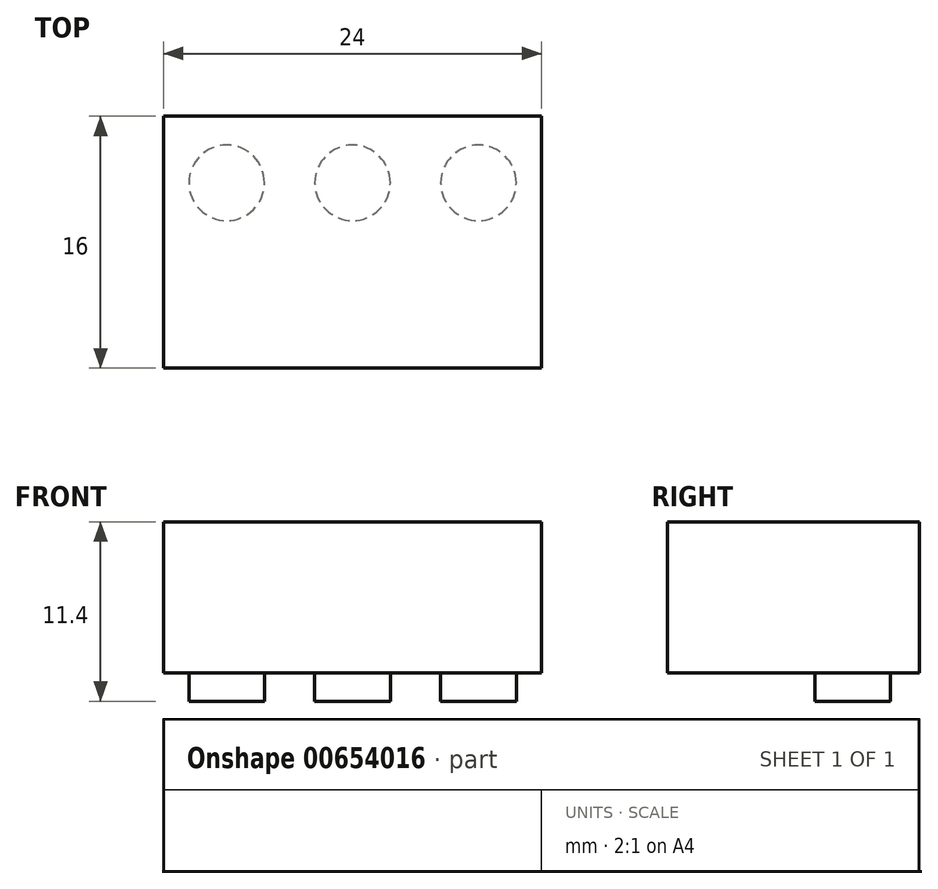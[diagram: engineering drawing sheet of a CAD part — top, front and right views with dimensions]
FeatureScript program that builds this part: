
annotation { "Feature Type Name" : "Feature", "Feature Type Description" : "" }
export const myFeature = defineFeature(function(context is Context, id is Id, definition is map)
    precondition{}
    {
        {
            var Q0;
            Q0=qCreatedBy(makeId("Top.planeOp"),FACE);
            var sketch = newSketch(context, id + "F0", { "sketchPlane" : qUnion([Q0])});
            skLineSegment(sketch, "E0.bottom", {"start": v(0, 0) * mm, "end": v(-24, 0) * mm});
            skLineSegment(sketch, "E0.top", {"start": v(0, 16) * mm, "end": v(-24, 16) * mm});
            skLineSegment(sketch, "E0.left", {"start": v(0, 0) * mm, "end": v(0, 16) * mm});
            skLineSegment(sketch, "E0.right", {"start": v(-24, 0) * mm, "end": v(-24, 16) * mm});
            skSolve(sketch);
        }
        {
            var Q0;
            Q0=makeQuery(id+"F0.imprint","IMPRINT",FACE,{"disambiguationData":[TD([[makeQuery(id+"F0.imprint","IMPRINT",EDGE,{"derivedFrom":sQuery(id+"F0.wireOp",EDGE,"E0.bottom")}),-1.0]])]});
            extrude(context, id + "F1", {"entities" : qUnion([Q0]), "depth" : 9.6 * mm, "offsetDistance" : 25.4 * mm});
        }
        {
            var Q0;
            Q0=qCreatedBy(makeId("Top.planeOp"),FACE);
            var sketch = newSketch(context, id + "F2", { "sketchPlane" : qUnion([Q0])});
            skLineSegment(sketch, "E1", {"start": v(-24.04, 7.52) * mm, "end": v(0, 7.52) * mm, "construction": true});
            skLineSegment(sketch, "E2", {"start": v(-16, 15.97) * mm, "end": v(-16, 0) * mm});
            skLineSegment(sketch, "E3", {"start": v(-8, 16.03) * mm, "end": v(-8, 0) * mm, "construction": true});
            skLineSegment(sketch, "E4", {"start": v(-23.99, 16.03) * mm, "end": v(-16, 7.52) * mm, "construction": true});
            skPoint(sketch, "E4.endSnap0", {"position": v(-16, 7.99) * mm});
            skLineSegment(sketch, "E5", {"start": v(-16, 7.52) * mm, "end": v(-8, 16.03) * mm, "construction": true});
            skLineSegment(sketch, "E6", {"start": v(-8, 16.03) * mm, "end": v(0, 7.52) * mm, "construction": true});
            skCircle(sketch, "E7", {"center": v(-20, 11.77) * mm, "radius": 2.4 * mm});
            skCircle(sketch, "E8", {"center": v(-12, 11.77) * mm, "radius": 2.4 * mm});
            skCircle(sketch, "E9", {"center": v(-4, 11.77) * mm, "radius": 2.4 * mm});
            skCircle(sketch, "E10.MirrorC", {"center": v(-20, 3.26) * mm, "radius": 2.4 * mm});
            skCircle(sketch, "E11.MirrorC", {"center": v(-12, 3.26) * mm, "radius": 2.4 * mm});
            skCircle(sketch, "E12.MirrorC", {"center": v(-4, 3.26) * mm, "radius": 2.4 * mm});
            skSolve(sketch);
        }
        {
            var Q0;
            Q0=makeQuery(id+"F2.imprint","IMPRINT",FACE,{"disambiguationData":[TD([[makeQuery(id+"F2.imprint","IMPRINT",EDGE,{"derivedFrom":sQuery(id+"F2.wireOp",EDGE,"E10.MirrorC")}),-1.0]])]});
            var Q1;
            Q1=makeQuery(id+"F2.imprint","IMPRINT",FACE,{"disambiguationData":[TD([[makeQuery(id+"F2.imprint","IMPRINT",EDGE,{"derivedFrom":sQuery(id+"F2.wireOp",EDGE,"E11.MirrorC")}),-1.0]])]});
            var Q2;
            Q2=makeQuery(id+"F2.imprint","IMPRINT",FACE,{"disambiguationData":[TD([[makeQuery(id+"F2.imprint","IMPRINT",EDGE,{"derivedFrom":sQuery(id+"F2.wireOp",EDGE,"E12.MirrorC")}),-1.0]])]});
            var Q3;
            Q3=makeQuery(id+"F2.imprint","IMPRINT",FACE,{"disambiguationData":[TD([[makeQuery(id+"F2.imprint","IMPRINT",EDGE,{"derivedFrom":sQuery(id+"F2.wireOp",EDGE,"E7")}),1.0]])]});
            var Q4;
            Q4=makeQuery(id+"F2.imprint","IMPRINT",FACE,{"disambiguationData":[TD([[makeQuery(id+"F2.imprint","IMPRINT",EDGE,{"derivedFrom":sQuery(id+"F2.wireOp",EDGE,"E8")}),1.0]])]});
            var Q5;
            Q5=makeQuery(id+"F2.imprint","IMPRINT",FACE,{"disambiguationData":[TD([[makeQuery(id+"F2.imprint","IMPRINT",EDGE,{"derivedFrom":sQuery(id+"F2.wireOp",EDGE,"E9")}),1.0]])]});
            extrude(context, id + "F3", {"entities" : qUnion([Q0, Q1, Q2, Q3, Q4, Q5]), "operationType" : NewBodyOperationType.ADD, "oppositeDirection" : true, "depth" : 1.8 * mm, "offsetDistance" : 25.4 * mm});
        }
    });
